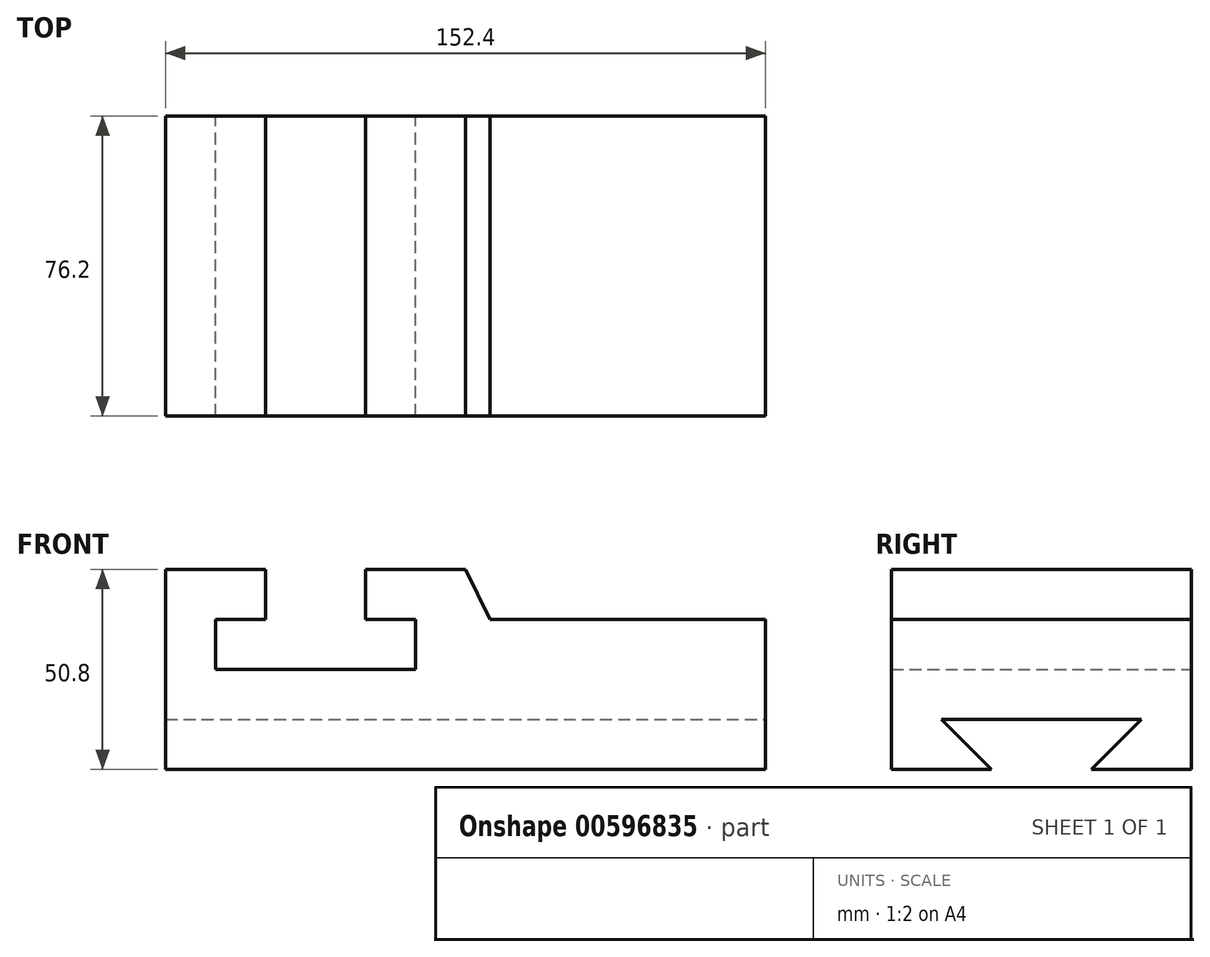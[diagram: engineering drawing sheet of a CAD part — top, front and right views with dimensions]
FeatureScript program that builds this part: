
annotation { "Feature Type Name" : "Feature", "Feature Type Description" : "" }
export const myFeature = defineFeature(function(context is Context, id is Id, definition is map)
    precondition{}
    {
        {
            var Q0;
            Q0=qCreatedBy(makeId("Front.planeOp"),FACE);
            var sketch = newSketch(context, id + "F0", { "sketchPlane" : qUnion([Q0])});
            skLineSegment(sketch, "E0", {"start": v(0, 0) * mm, "end": v(0, 50.8) * mm});
            skLineSegment(sketch, "E1", {"start": v(0, 50.8) * mm, "end": v(25.4, 50.8) * mm});
            skLineSegment(sketch, "E2", {"start": v(25.4, 50.8) * mm, "end": v(25.4, 38.1) * mm});
            skLineSegment(sketch, "E3", {"start": v(25.4, 38.1) * mm, "end": v(12.7, 38.1) * mm});
            skLineSegment(sketch, "E4", {"start": v(12.7, 38.1) * mm, "end": v(12.7, 25.4) * mm});
            skLineSegment(sketch, "E5", {"start": v(12.7, 25.4) * mm, "end": v(63.5, 25.4) * mm});
            skLineSegment(sketch, "E6", {"start": v(63.5, 25.4) * mm, "end": v(63.5, 38.1) * mm});
            skLineSegment(sketch, "E7", {"start": v(63.5, 38.1) * mm, "end": v(50.8, 38.1) * mm});
            skLineSegment(sketch, "E8", {"start": v(50.8, 38.1) * mm, "end": v(50.8, 50.8) * mm});
            skLineSegment(sketch, "E9", {"start": v(50.8, 50.8) * mm, "end": v(76.2, 50.8) * mm});
            skLineSegment(sketch, "E10", {"start": v(152.4, 38.1) * mm, "end": v(152.4, 0) * mm});
            skLineSegment(sketch, "E11", {"start": v(152.4, 0) * mm, "end": v(0, 0) * mm});
            skLineSegment(sketch, "E12", {"start": v(76.2, 50.8) * mm, "end": v(82.43, 38.1) * mm});
            skLineSegment(sketch, "E13", {"start": v(82.43, 38.1) * mm, "end": v(152.4, 38.1) * mm});
            skLineSegment(sketch, "E14", {"start": v(25.4, 50.8) * mm, "end": v(50.8, 50.8) * mm});
            skLineSegment(sketch, "E15", {"start": v(76.2, 50.8) * mm, "end": v(152.4, 50.8) * mm});
            skLineSegment(sketch, "E16", {"start": v(152.4, 50.8) * mm, "end": v(152.4, 38.1) * mm});
            skLineSegment(sketch, "E17", {"start": v(12.7, 25.4) * mm, "end": v(0, 25.4) * mm});
            skLineSegment(sketch, "E18", {"start": v(82.55, 50.8) * mm, "end": v(76.2, 50.8) * mm});
            skLineSegment(sketch, "E19", {"start": v(76.2, 50.8) * mm, "end": v(82.55, 50.8) * mm});
            skLineSegment(sketch, "E20", {"start": v(82.43, 38.1) * mm, "end": v(82.55, 50.8) * mm});
            skSolve(sketch);
        }
        {
            var Q0;
            Q0=makeQuery(id+"F0.imprint","IMPRINT",FACE,{"disambiguationData":[TD([[makeQuery(id+"F0.imprint","IMPRINT",EDGE,{"derivedFrom":sQuery(id+"F0.wireOp",EDGE,"E5")}),-1.0]])]});
            var Q1;
            {var subQ0=sQuery(id+"F0.wireOp",EDGE,"E1");Q1=makeQuery(id+"F0.imprint","IMPRINT",FACE,{"disambiguationData":[TD([[makeQuery(id+"F0.imprint","IMPRINT",EDGE,{"derivedFrom":subQ0}),-1.0]])]});}
            extrude(context, id + "F1", {"entities" : qUnion([Q0, Q1]), "depth" : 76.2 * mm, "offsetDistance" : 25.4 * mm});
        }
        {
            var Q0;
            Q0=makeQuery(id+"F1.opExtrude","SWEPT_FACE",FACE,{"disambiguationData":[OSD([sQuery(id+"F0.wireOp",EDGE,"E10")])]});
            var sketch = newSketch(context, id + "F2", { "sketchPlane" : qUnion([Q0])});
            skLineSegment(sketch, "E21", {"start": v(-76.2, 0) * mm, "end": v(-50.8, 0) * mm});
            skLineSegment(sketch, "E22", {"start": v(-25.4, 0) * mm, "end": v(0, 0) * mm});
            skLineSegment(sketch, "E23", {"start": v(-50.8, 0) * mm, "end": v(-63.5, 12.7) * mm});
            skLineSegment(sketch, "E24", {"start": v(-63.5, 12.7) * mm, "end": v(-12.7, 12.7) * mm});
            skLineSegment(sketch, "E25", {"start": v(-12.7, 12.7) * mm, "end": v(-25.4, 0) * mm});
            skSolve(sketch);
        }
        {
            var Q0;
            {var subQ0=sQuery(id+"F2.wireOp",EDGE,"E23");Q0=makeQuery(id+"F2.imprint","IMPRINT",FACE,{"disambiguationData":[TD([[makeQuery(id+"F2.imprint","IMPRINT",EDGE,{"derivedFrom":subQ0}),-1.0]])]});}
            extrude(context, id + "F3", {"entities" : qUnion([Q0]), "operationType" : NewBodyOperationType.REMOVE, "oppositeDirection" : true, "depth" : 152.4 * mm, "offsetDistance" : 25.4 * mm});
        }
    });
